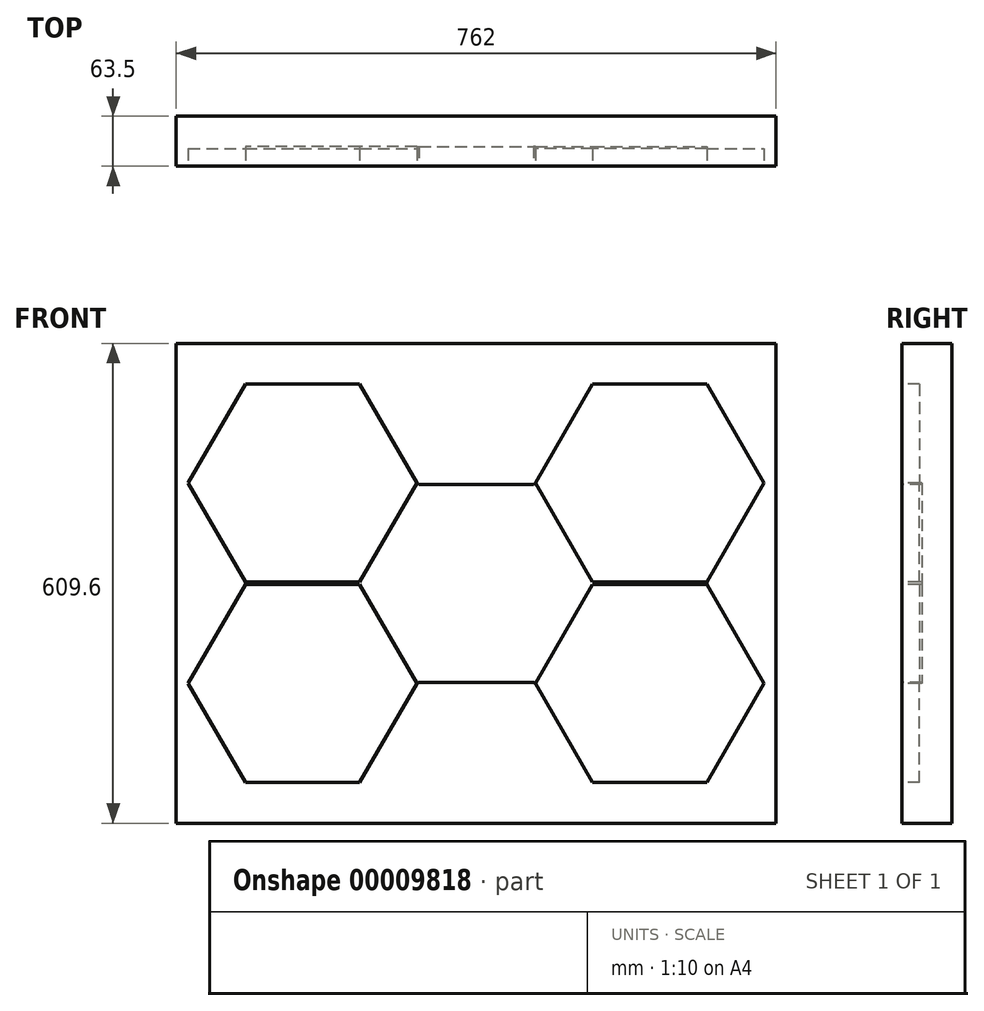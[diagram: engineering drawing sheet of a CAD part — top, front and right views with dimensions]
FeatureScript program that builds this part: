
annotation { "Feature Type Name" : "Feature", "Feature Type Description" : "" }
export const myFeature = defineFeature(function(context is Context, id is Id, definition is map)
    precondition{}
    {
        {
            var Q0;
            Q0=qCreatedBy(makeId("Front.planeOp"),FACE);
            var sketch = newSketch(context, id + "F0", { "sketchPlane" : qUnion([Q0])});
            skLineSegment(sketch, "E0.bottom", {"start": v(0, 609.6) * mm, "end": v(762, 609.6) * mm});
            skLineSegment(sketch, "E0.top", {"start": v(0, 0) * mm, "end": v(762, 0) * mm});
            skLineSegment(sketch, "E0.left", {"start": v(0, 609.6) * mm, "end": v(0, 0) * mm});
            skLineSegment(sketch, "E0.right", {"start": v(762, 609.6) * mm, "end": v(762, 0) * mm});
            skSolve(sketch);
        }
        {
            var Q0;
            Q0 = qSketchRegion(id + "F0", true);
            extrude(context, id + "F1", {"entities" : qUnion([Q0]), "depth" : 63.5 * mm});
        }
        {
            var Q0;
            Q0=makeQuery(id+"F1.opExtrude","CAP_FACE",FACE,{"disambiguationData":[OSD([sQuery(id+"F0.wireOp",EDGE,"E0.bottom"),sQuery(id+"F0.wireOp",EDGE,"E0.top"),sQuery(id+"F0.wireOp",EDGE,"E0.left"),sQuery(id+"F0.wireOp",EDGE,"E0.right")])],"isStart":false});
            var sketch = newSketch(context, id + "F2", { "sketchPlane" : qUnion([Q0])});
            skCircle(sketch, "E1.cCircle", {"center": v(381, 304.8) * mm, "radius": 125.73 * mm, "construction": true});
            skLineSegment(sketch, "E1.0", {"start": v(453.6, 430.53) * mm, "end": v(526.18, 304.8) * mm});
            skLineSegment(sketch, "E1.1", {"start": v(526.18, 304.8) * mm, "end": v(453.6, 179.07) * mm});
            skLineSegment(sketch, "E1.2", {"start": v(453.6, 179.07) * mm, "end": v(308.4, 179.07) * mm});
            skLineSegment(sketch, "E1.3", {"start": v(308.4, 179.07) * mm, "end": v(235.82, 304.8) * mm});
            skLineSegment(sketch, "E1.4", {"start": v(235.82, 304.8) * mm, "end": v(308.4, 430.53) * mm});
            skLineSegment(sketch, "E1.5", {"start": v(308.4, 430.53) * mm, "end": v(453.6, 430.53) * mm});
            skPoint(sketch, "E1.0.midPoint", {"position": v(489.89, 367.66) * mm});
            skPoint(sketch, "E2", {"position": v(381, 609.6) * mm});
            skCircle(sketch, "E3.cCircle", {"center": v(160.48, 432.12) * mm, "radius": 125.73 * mm, "construction": true});
            skLineSegment(sketch, "E3.0", {"start": v(233.07, 306.39) * mm, "end": v(87.89, 306.39) * mm});
            skLineSegment(sketch, "E3.1", {"start": v(87.89, 306.39) * mm, "end": v(15.3, 432.12) * mm});
            skLineSegment(sketch, "E3.2", {"start": v(15.3, 432.12) * mm, "end": v(87.89, 557.85) * mm});
            skLineSegment(sketch, "E3.3", {"start": v(87.89, 557.85) * mm, "end": v(233.07, 557.85) * mm});
            skLineSegment(sketch, "E3.4", {"start": v(233.07, 557.85) * mm, "end": v(305.66, 432.12) * mm});
            skLineSegment(sketch, "E3.5", {"start": v(305.66, 432.12) * mm, "end": v(233.07, 306.39) * mm});
            skPoint(sketch, "E3.0.midPoint", {"position": v(160.48, 306.39) * mm});
            skCircle(sketch, "E4.cCircle", {"center": v(160.48, 177.48) * mm, "radius": 125.73 * mm, "construction": true});
            skLineSegment(sketch, "E4.0", {"start": v(233.07, 303.21) * mm, "end": v(305.66, 177.48) * mm});
            skLineSegment(sketch, "E4.1", {"start": v(305.66, 177.48) * mm, "end": v(233.07, 51.75) * mm});
            skLineSegment(sketch, "E4.2", {"start": v(233.07, 51.75) * mm, "end": v(87.89, 51.75) * mm});
            skLineSegment(sketch, "E4.3", {"start": v(87.89, 51.75) * mm, "end": v(15.3, 177.48) * mm});
            skLineSegment(sketch, "E4.4", {"start": v(15.3, 177.48) * mm, "end": v(87.89, 303.21) * mm});
            skLineSegment(sketch, "E4.5", {"start": v(87.89, 303.21) * mm, "end": v(233.07, 303.21) * mm});
            skPoint(sketch, "E4.0.midPoint", {"position": v(269.36, 240.35) * mm});
            skCircle(sketch, "E5.cCircle", {"center": v(601.52, 432.12) * mm, "radius": 125.73 * mm, "construction": true});
            skLineSegment(sketch, "E5.0", {"start": v(674.11, 306.39) * mm, "end": v(528.93, 306.39) * mm});
            skLineSegment(sketch, "E5.1", {"start": v(528.93, 306.39) * mm, "end": v(456.34, 432.12) * mm});
            skLineSegment(sketch, "E5.2", {"start": v(456.34, 432.12) * mm, "end": v(528.93, 557.85) * mm});
            skLineSegment(sketch, "E5.3", {"start": v(528.93, 557.85) * mm, "end": v(674.11, 557.85) * mm});
            skLineSegment(sketch, "E5.4", {"start": v(674.11, 557.85) * mm, "end": v(746.7, 432.12) * mm});
            skLineSegment(sketch, "E5.5", {"start": v(746.7, 432.12) * mm, "end": v(674.11, 306.39) * mm});
            skPoint(sketch, "E5.0.midPoint", {"position": v(601.52, 306.39) * mm});
            skCircle(sketch, "E6.cCircle", {"center": v(601.52, 177.48) * mm, "radius": 125.73 * mm, "construction": true});
            skLineSegment(sketch, "E6.0", {"start": v(674.11, 303.21) * mm, "end": v(746.7, 177.48) * mm});
            skLineSegment(sketch, "E6.1", {"start": v(746.7, 177.48) * mm, "end": v(674.11, 51.75) * mm});
            skLineSegment(sketch, "E6.2", {"start": v(674.11, 51.75) * mm, "end": v(528.93, 51.75) * mm});
            skLineSegment(sketch, "E6.3", {"start": v(528.93, 51.75) * mm, "end": v(456.34, 177.48) * mm});
            skLineSegment(sketch, "E6.4", {"start": v(456.34, 177.48) * mm, "end": v(528.93, 303.21) * mm});
            skLineSegment(sketch, "E6.5", {"start": v(528.93, 303.21) * mm, "end": v(674.11, 303.21) * mm});
            skPoint(sketch, "E6.0.midPoint", {"position": v(710.4, 240.35) * mm});
            skPoint(sketch, "E7", {"position": v(0, 304.8) * mm});
            skSolve(sketch);
        }
        {
            var Q0;
            Q0=makeQuery(id+"F2.imprint","IMPRINT",FACE,{"disambiguationData":[TD([[makeQuery(id+"F2.imprint","IMPRINT",EDGE,{"derivedFrom":sQuery(id+"F2.wireOp",EDGE,"E1.0")}),-1.0]])]});
            extrude(context, id + "F3", {"entities" : qUnion([Q0]), "operationType" : NewBodyOperationType.REMOVE, "oppositeDirection" : true, "depth" : 25.15 * mm});
        }
        {
            var Q0;
            Q0=makeQuery(id+"F2.imprint","IMPRINT",FACE,{"disambiguationData":[TD([[makeQuery(id+"F2.imprint","IMPRINT",EDGE,{"derivedFrom":sQuery(id+"F2.wireOp",EDGE,"E3.0")}),-1.0]])]});
            var Q1;
            Q1=makeQuery(id+"F2.imprint","IMPRINT",FACE,{"disambiguationData":[TD([[makeQuery(id+"F2.imprint","IMPRINT",EDGE,{"derivedFrom":sQuery(id+"F2.wireOp",EDGE,"E4.0")}),-1.0]])]});
            var Q2;
            Q2=makeQuery(id+"F2.imprint","IMPRINT",FACE,{"disambiguationData":[TD([[makeQuery(id+"F2.imprint","IMPRINT",EDGE,{"derivedFrom":sQuery(id+"F2.wireOp",EDGE,"E5.0")}),-1.0]])]});
            var Q3;
            Q3=makeQuery(id+"F2.imprint","IMPRINT",FACE,{"disambiguationData":[TD([[makeQuery(id+"F2.imprint","IMPRINT",EDGE,{"derivedFrom":sQuery(id+"F2.wireOp",EDGE,"E6.0")}),-1.0]])]});
            extrude(context, id + "F4", {"entities" : qUnion([Q0, Q1, Q2, Q3]), "operationType" : NewBodyOperationType.REMOVE, "oppositeDirection" : true, "depth" : 22.22 * mm});
        }
        {
            var Q0;
            Q0=makeQuery(id+"F2.imprint","IMPRINT",FACE,{"disambiguationData":[TD([[makeQuery(id+"F2.imprint","IMPRINT",EDGE,{"derivedFrom":sQuery(id+"F2.wireOp",EDGE,"E1.0")}),1.0]])]});
            var sketch = newSketch(context, id + "F5", { "sketchPlane" : qUnion([Q0])});
            skLineSegment(sketch, "E8", {"start": v(87.89, 306.39) * mm, "end": v(87.89, 303.21) * mm});
            skLineSegment(sketch, "E9", {"start": v(305.66, 432.12) * mm, "end": v(308.4, 430.53) * mm});
            skLineSegment(sketch, "E10", {"start": v(305.66, 177.48) * mm, "end": v(308.4, 179.07) * mm});
            skLineSegment(sketch, "E11", {"start": v(453.6, 430.53) * mm, "end": v(456.34, 432.12) * mm});
            skLineSegment(sketch, "E12", {"start": v(674.11, 306.39) * mm, "end": v(674.11, 303.21) * mm});
            skLineSegment(sketch, "E13", {"start": v(456.34, 177.48) * mm, "end": v(453.6, 179.07) * mm});
            skLineSegment(sketch, "E14", {"start": v(87.89, 306.39) * mm, "end": v(233.07, 306.39) * mm});
            skLineSegment(sketch, "E15", {"start": v(233.07, 306.39) * mm, "end": v(305.66, 432.12) * mm});
            skLineSegment(sketch, "E16", {"start": v(87.89, 303.21) * mm, "end": v(233.07, 303.21) * mm});
            skLineSegment(sketch, "E17", {"start": v(233.07, 303.21) * mm, "end": v(305.66, 177.48) * mm});
            skLineSegment(sketch, "E18", {"start": v(308.4, 179.07) * mm, "end": v(235.82, 304.8) * mm});
            skLineSegment(sketch, "E19", {"start": v(235.82, 304.8) * mm, "end": v(308.4, 430.53) * mm});
            skLineSegment(sketch, "E20", {"start": v(456.34, 432.12) * mm, "end": v(528.93, 306.39) * mm});
            skLineSegment(sketch, "E21", {"start": v(528.93, 306.39) * mm, "end": v(674.11, 306.39) * mm});
            skLineSegment(sketch, "E22", {"start": v(453.6, 430.53) * mm, "end": v(526.18, 304.8) * mm});
            skLineSegment(sketch, "E23", {"start": v(526.18, 304.8) * mm, "end": v(453.6, 179.07) * mm});
            skLineSegment(sketch, "E24", {"start": v(456.34, 177.48) * mm, "end": v(528.93, 303.21) * mm});
            skLineSegment(sketch, "E25", {"start": v(528.93, 303.21) * mm, "end": v(674.11, 303.21) * mm});
            skSolve(sketch);
        }
        {
            var Q0;
            Q0 = qSketchRegion(id + "F5", true);
            extrude(context, id + "F6", {"entities" : qUnion([Q0]), "operationType" : NewBodyOperationType.REMOVE, "oppositeDirection" : true, "depth" : 25.15 * mm});
        }
    });
